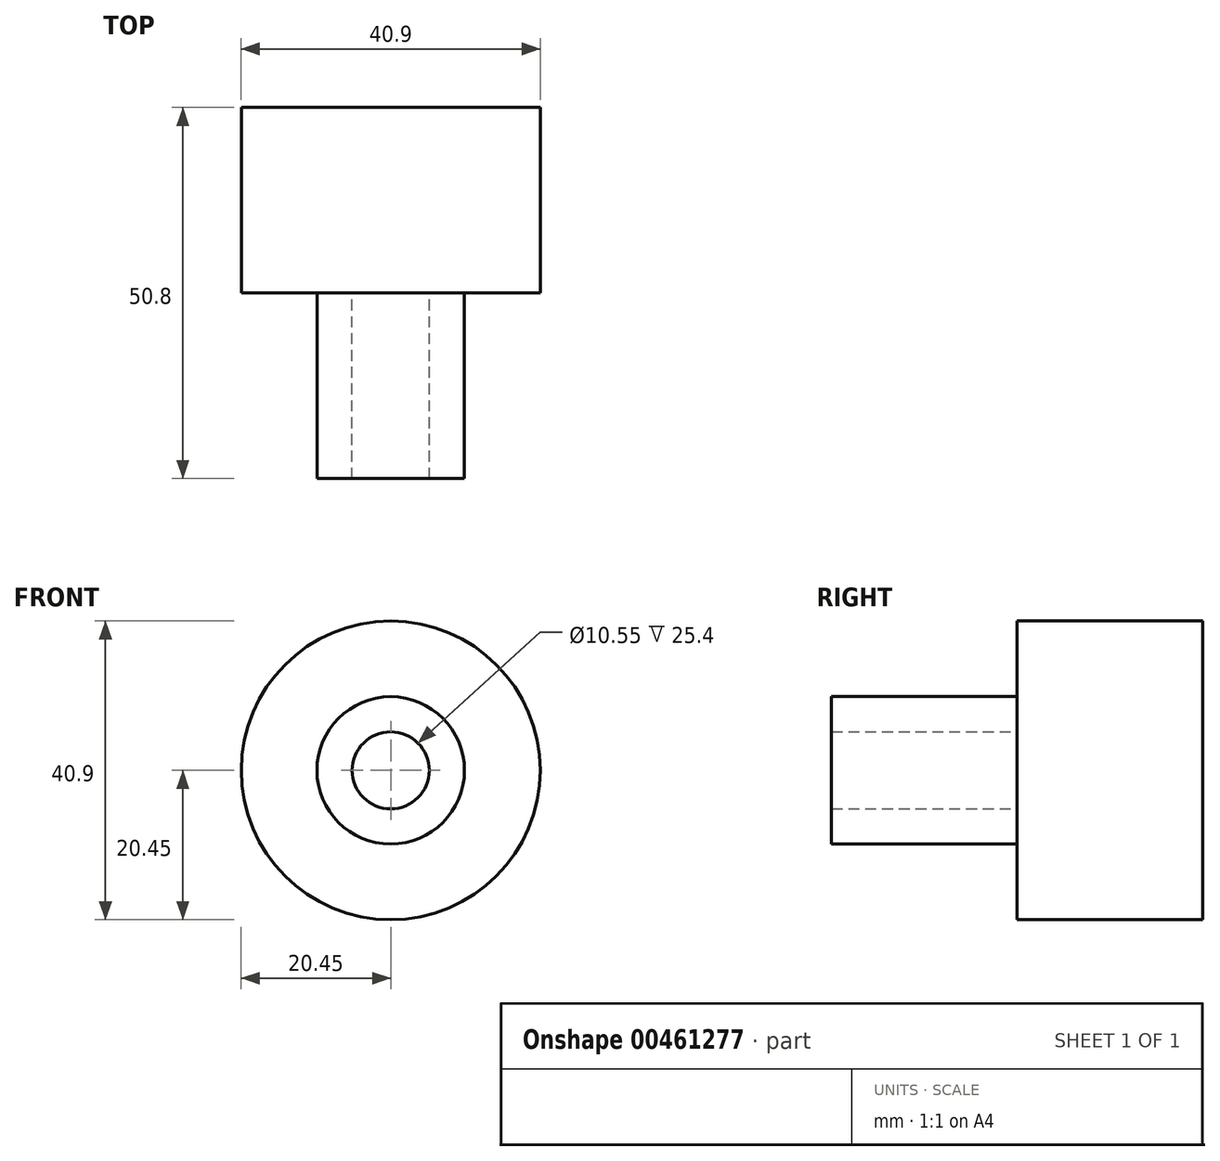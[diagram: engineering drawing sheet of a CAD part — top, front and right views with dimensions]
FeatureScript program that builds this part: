
annotation { "Feature Type Name" : "Feature", "Feature Type Description" : "" }
export const myFeature = defineFeature(function(context is Context, id is Id, definition is map)
    precondition{}
    {
        {
            var Q0;
            Q0=qCreatedBy(makeId("Front.planeOp"),FACE);
            var sketch = newSketch(context, id + "F0", { "sketchPlane" : qUnion([Q0])});
            skCircle(sketch, "E0", {"center": v(0, 0) * mm, "radius": 20.45 * mm});
            skCircle(sketch, "E1", {"center": v(0, 0) * mm, "radius": 10.09 * mm});
            skCircle(sketch, "E2", {"center": v(0, 0) * mm, "radius": 5.28 * mm});
            skSolve(sketch);
        }
        {
            var Q0;
            Q0=makeQuery(id+"F0.imprint","IMPRINT",FACE,{"disambiguationData":[TD([[makeQuery(id+"F0.imprint","IMPRINT",EDGE,{"derivedFrom":sQuery(id+"F0.wireOp",EDGE,"E0")}),1.0]])]});
            var Q1;
            Q1=makeQuery(id+"F0.imprint","IMPRINT",FACE,{"disambiguationData":[TD([[makeQuery(id+"F0.imprint","IMPRINT",EDGE,{"derivedFrom":sQuery(id+"F0.wireOp",EDGE,"E1")}),1.0]])]});
            var Q2;
            Q2=makeQuery(id+"F0.imprint","IMPRINT",FACE,{"disambiguationData":[TD([[makeQuery(id+"F0.imprint","IMPRINT",EDGE,{"derivedFrom":sQuery(id+"F0.wireOp",EDGE,"E2")}),1.0]])]});
            extrude(context, id + "F1", {"entities" : qUnion([Q0, Q1, Q2]), "depth" : 25.4 * mm});
        }
        {
            var Q0;
            Q0=makeQuery(id+"F0.imprint","IMPRINT",FACE,{"disambiguationData":[TD([[makeQuery(id+"F0.imprint","IMPRINT",EDGE,{"derivedFrom":sQuery(id+"F0.wireOp",EDGE,"E1")}),1.0]])]});
            extrude(context, id + "F2", {"entities" : qUnion([Q0]), "operationType" : NewBodyOperationType.ADD, "depth" : 50.8 * mm});
        }
    });
